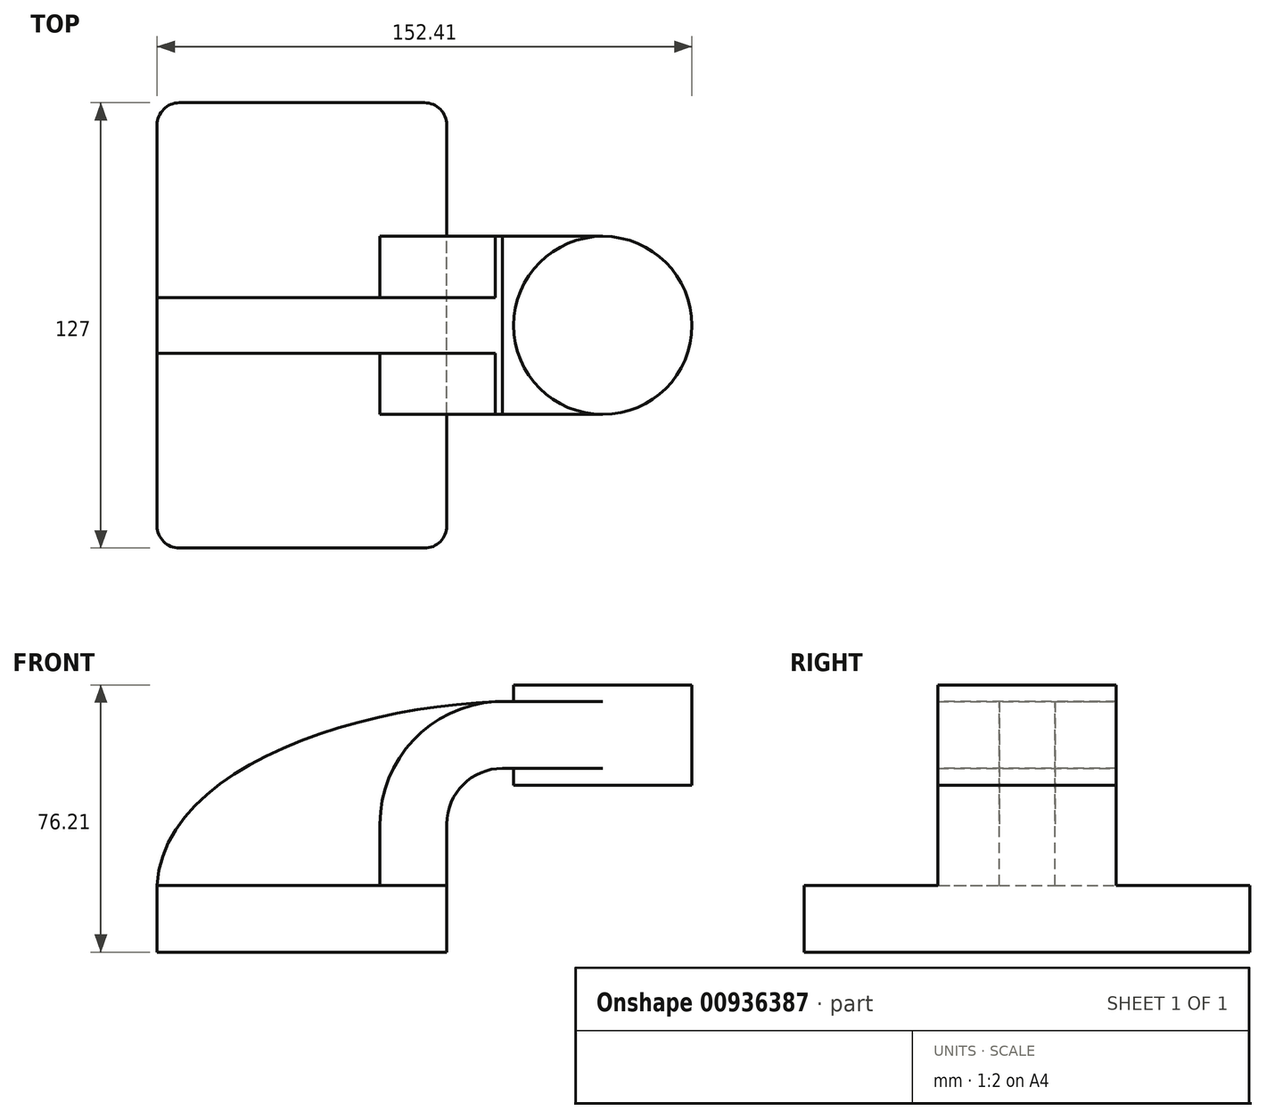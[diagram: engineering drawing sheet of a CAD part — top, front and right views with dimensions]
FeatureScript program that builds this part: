
annotation { "Feature Type Name" : "Feature", "Feature Type Description" : "" }
export const myFeature = defineFeature(function(context is Context, id is Id, definition is map)
    precondition{}
    {
        {
            var Q0;
            Q0=qCreatedBy(makeId("Front.planeOp"),FACE);
            var sketch = newSketch(context, id + "F0", { "sketchPlane" : qUnion([Q0])});
            skLineSegment(sketch, "E0.bottom", {"start": v(41.28, -9.52) * mm, "end": v(-41.28, -9.53) * mm});
            skLineSegment(sketch, "E0.top", {"start": v(41.28, 9.53) * mm, "end": v(-41.28, 9.53) * mm});
            skLineSegment(sketch, "E0.left", {"start": v(41.28, -9.52) * mm, "end": v(41.28, 9.53) * mm});
            skLineSegment(sketch, "E0.right", {"start": v(-41.28, -9.53) * mm, "end": v(-41.28, 9.53) * mm});
            skPoint(sketch, "E0.middle", {"position": v(0, 0) * mm});
            skLineSegment(sketch, "E1.bottom", {"start": v(60.32, 66.68) * mm, "end": v(111.12, 66.68) * mm});
            skLineSegment(sketch, "E1.top", {"start": v(60.32, 38.1) * mm, "end": v(111.12, 38.1) * mm});
            skLineSegment(sketch, "E1.left", {"start": v(60.32, 66.68) * mm, "end": v(60.32, 38.1) * mm});
            skLineSegment(sketch, "E1.right", {"start": v(111.12, 66.68) * mm, "end": v(111.12, 38.1) * mm});
            skPoint(sketch, "E1.middle", {"position": v(85.72, 52.39) * mm});
            skLineSegment(sketch, "E2", {"start": v(41.28, 9.53) * mm, "end": v(41.28, 27) * mm});
            skArc(sketch, "E3", {"start": v(41.27, 27) * mm, "mid": v(45.92, 38.23) * mm, "end": v(57.15, 42.88) * mm});
            skLineSegment(sketch, "E4", {"start": v(57.15, 42.88) * mm, "end": v(85.72, 42.88) * mm});
            skLineSegment(sketch, "E5.0", {"start": v(57.15, 61.93) * mm, "end": v(85.72, 61.93) * mm});
            skArc(sketch, "E5.1", {"start": v(22.23, 27) * mm, "mid": v(32.45, 51.7) * mm, "end": v(57.15, 61.93) * mm});
            skLineSegment(sketch, "E5.2", {"start": v(22.22, 9.53) * mm, "end": v(22.22, 27) * mm});
            skLineSegment(sketch, "E6", {"start": v(85.72, 66.68) * mm, "end": v(85.72, 38.1) * mm});
            skFitSpline(sketch, "E7", {"points": [v(-41.28, 9.52) * mm, v(57.15, 61.93) * mm], "startDerivative": vector(5, 100.58) * mm, "endDerivative": vector(123.5, 2.92) * mm});
            skSolve(sketch);
        }
        {
            var Q0;
            Q0=makeQuery(id+"F0.imprint","IMPRINT",FACE,{"disambiguationData":[TD([[makeQuery(id+"F0.imprint","IMPRINT",EDGE,{"derivedFrom":sQuery(id+"F0.wireOp",EDGE,"E0.bottom")}),-1.0]])]});
            extrude(context, id + "F1", {"entities" : qUnion([Q0]), "depth" : 127 * mm, "offsetDistance" : 25.4 * mm, "symmetric" : true});
        }
        {
            var Q0;
            {var subQ1=sQuery(id+"F0.wireOp",EDGE,"E2");Q0=makeQuery(id+"F0.imprint","IMPRINT",FACE,{"disambiguationData":[TD([[makeQuery(id+"F0.imprint","IMPRINT",EDGE,{"derivedFrom":subQ1}),1.0]])]});}
            var Q1;
            {var subQ0=sQuery(id+"F0.wireOp",EDGE,"E5.0");var subQ1=sQuery(id+"F0.wireOp",EDGE,"E1.left");var subQ2=makeQuery(id+"F0.imprint","INTERSECT",VERTEX,{"derivedFrom":[subQ1,subQ0]});Q1=makeQuery(id+"F0.imprint","IMPRINT",FACE,{"disambiguationData":[TD([[makeQuery(id+"F0.imprint","IMPRINT",EDGE,{"disambiguationData":[TD([[subQ2,-1.0]])],"derivedFrom":subQ1}),1.0]])]});}
            extrude(context, id + "F2", {"entities" : qUnion([Q0, Q1]), "operationType" : NewBodyOperationType.ADD, "depth" : 50.8 * mm, "offsetDistance" : 25.4 * mm, "symmetric" : true});
        }
        {
            var Q0;
            {var subQ3=sQuery(id+"F0.wireOp",EDGE,"E5.2");Q0=makeQuery(id+"F0.imprint","IMPRINT",FACE,{"disambiguationData":[TD([[makeQuery(id+"F0.imprint","IMPRINT",EDGE,{"derivedFrom":subQ3}),1.0]])]});}
            extrude(context, id + "F3", {"entities" : qUnion([Q0]), "operationType" : NewBodyOperationType.ADD, "depth" : 15.88 * mm, "offsetDistance" : 25.4 * mm, "symmetric" : true});
        }
        {
            var Q0;
            {var subQ4=sQuery(id+"F0.wireOp",EDGE,"E1.right");Q0=makeQuery(id+"F0.imprint","IMPRINT",FACE,{"disambiguationData":[TD([[makeQuery(id+"F0.imprint","IMPRINT",EDGE,{"derivedFrom":subQ4}),-1.0]])]});}
            var Q1;
            Q1=sQuery(id+"F0.wireOp",EDGE,"E6");
            revolve(context, id + "F4", {"operationType" : NewBodyOperationType.ADD, "surfaceOperationType" : NewSurfaceOperationType.NEW, "entities" : qUnion([Q0]), "axis" : qUnion([Q1]), "revolveType" : RevolveType.FULL});
        }
        {
            var Q0;
            Q0=makeQuery(id+"F1.opExtrude","CAP_EDGE",EDGE,{"disambiguationData":[OSD([sQuery(id+"F0.wireOp",EDGE,"E0.left")])],"isStart":false});
            var Q1;
            Q1=makeQuery(id+"F1.opExtrude","CAP_EDGE",EDGE,{"disambiguationData":[OSD([sQuery(id+"F0.wireOp",EDGE,"E0.right")])],"isStart":false});
            var Q2;
            Q2=makeQuery(id+"F1.opExtrude","CAP_EDGE",EDGE,{"disambiguationData":[OSD([sQuery(id+"F0.wireOp",EDGE,"E0.left")])],"isStart":true});
            var Q3;
            Q3=makeQuery(id+"F1.opExtrude","CAP_EDGE",EDGE,{"disambiguationData":[OSD([sQuery(id+"F0.wireOp",EDGE,"E0.right")])],"isStart":true});
            fillet(context, id + "F5", {"entities" : qUnion([Q0, Q1, Q2, Q3]), "radius" : 6.35 * mm, "tangentPropagation" : true, "allowEdgeOverflow" : false});
        }
    });
